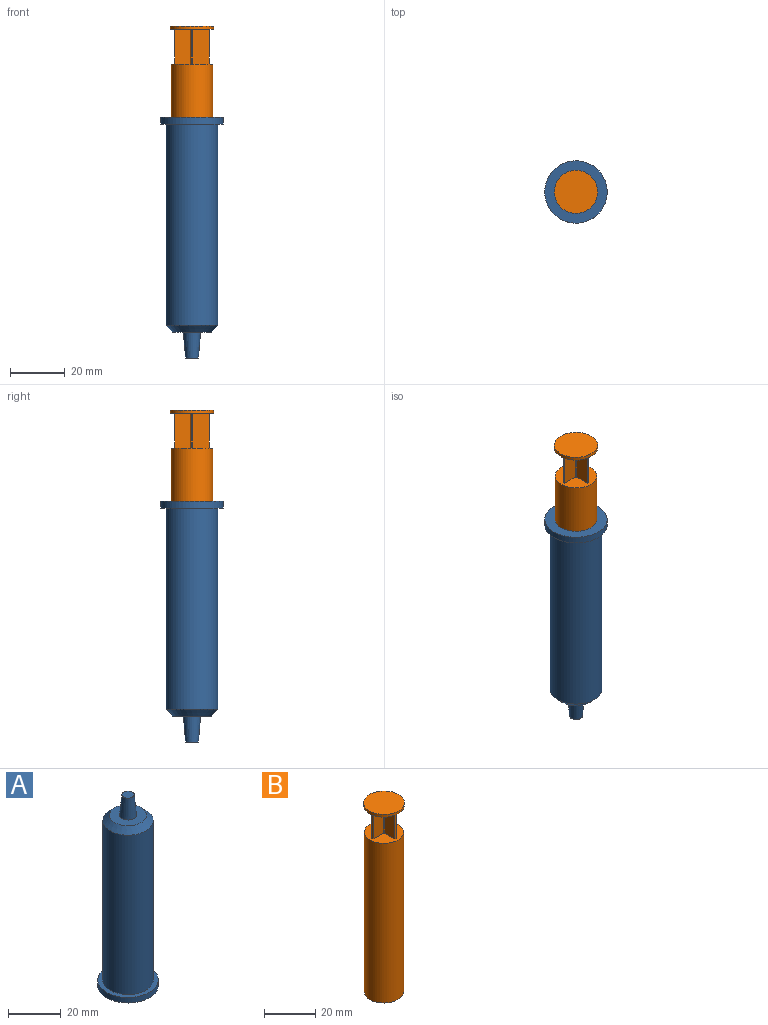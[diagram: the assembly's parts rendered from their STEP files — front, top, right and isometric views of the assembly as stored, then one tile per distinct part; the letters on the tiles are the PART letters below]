
ASSEMBLY  parts=2 mates=1
PART A: 10 faces, bbox 22.9x22.9x88.3 mm
  f0: cylinder r=9.53mm len=73.66mm, axis (0,0,-1), area 4408.4mm2, adj f4,f7
  f1: plane 13.97x13.97mm, normal (0,0,1), area 121.6mm2, adj f5,f7
  f2: cylinder r=11.43mm len=22.86mm, axis (0,0,1), area 182.4mm2, adj f3,f4
  f3: plane 22.86x22.86mm, normal (0,0,-1), area 228mm2, adj f2,f8
  f4: plane 22.86x22.86mm, normal (0,0,1), area 125.4mm2, adj f0,f2
  f5: cone r=3.17mm half-angle=5deg, axis (0,0,-1), area 165.7mm2, adj f1,f6
  f6: plane 4.68x4.68mm, normal (0,0,1), area 17.2mm2, adj f5
  f7: cone r=6.99mm half-angle=45deg, axis (0,0,-1), area 186.3mm2, adj f0,f1
  f8: cylinder r=7.62mm len=76.2mm, axis (0,0,-1), area 3648.3mm2, adj f3,f9
  f9: plane 15.24x15.24mm, normal (0,0,-1), area 182.4mm2, adj f8
PART B: 28 faces, bbox 15.9x15.9x90.2 mm
  f0: plane 15.24x15.24mm, normal (0,0,1), area 166.4mm2, adj f1,f3,f4,f5,f6,f7,f8,f9
  f1: cylinder r=7.62mm len=76.2mm, axis (0,0,-1), area 3648.3mm2, adj f0,f2
  f2: plane 15.24x15.24mm, normal (0,0,-1), area 182.4mm2, adj f1
  f3: plane 12.7x5.67mm, normal (-1,0,0), area 72mm2, adj f0,f4,f18,f19
  f4: cylinder r=0.75mm len=12.7mm, axis (0,0,-1), area 6.7mm2, adj f0,f3,f5,f19
  f5: plane 12.7x5.67mm, normal (0,1,0), area 72mm2, adj f0,f4,f6,f19
  f6: plane 12.7x0.64mm, normal (-1,0,0), area 8.1mm2, adj f0,f5,f7,f19
  f7: plane 12.7x5.67mm, normal (0,-1,0), area 72mm2, adj f0,f6,f8,f19
  f8: cylinder r=0.75mm len=12.7mm, axis (0,0,-1), area 6.7mm2, adj f0,f7,f9,f19
  f9: plane 12.7x5.67mm, normal (-1,0,0), area 72mm2, adj f0,f8,f10,f19
  f10: plane 12.7x0.64mm, normal (0,-1,0), area 8.1mm2, adj f0,f9,f11,f19
  f11: plane 12.7x5.67mm, normal (1,0,0), area 72mm2, adj f0,f10,f12,f19
  f12: cylinder r=0.75mm len=12.7mm, axis (0,0,-1), area 6.7mm2, adj f0,f11,f13,f19
  f13: plane 12.7x5.67mm, normal (0,-1,0), area 72mm2, adj f0,f12,f14,f19
  f14: plane 12.7x0.64mm, normal (1,0,0), area 8.1mm2, adj f0,f13,f15,f19
  f15: plane 12.7x5.67mm, normal (0,1,0), area 72mm2, adj f0,f14,f16,f19
  f16: cylinder r=0.75mm len=12.7mm, axis (0,0,-1), area 6.7mm2, adj f0,f15,f17,f19
  f17: plane 12.7x5.67mm, normal (1,0,0), area 72mm2, adj f0,f16,f18,f19
  f18: plane 12.7x0.64mm, normal (0,1,0), area 8.1mm2, adj f0,f3,f17,f19
  f19: plane 15.88x15.88mm, normal (0,0,-1), area 181.9mm2, adj f3,f4,f5,f6,f7,f8,f9,f10
  f20: cylinder r=7.94mm len=15.88mm, axis (0,0,-1), area 63.3mm2, adj f19,f21
  f21: plane 15.88x15.88mm, normal (0,0,1), area 197.9mm2, adj f20
  f22: plane 0.64x0.64mm, normal (0,0,1), area 0.4mm2, adj f23,f24,f25,f26
  f23: plane 12.7x0.64mm, normal (1,0,0), area 8.1mm2, adj f22,f24,f26,f27
  f24: plane 12.7x0.64mm, normal (0,1,0), area 8.1mm2, adj f22,f23,f25,f27
  f25: plane 12.7x0.64mm, normal (-1,0,0), area 8.1mm2, adj f22,f24,f26,f27
  f26: plane 12.7x0.64mm, normal (0,-1,0), area 8.1mm2, adj f22,f23,f25,f27
  f27: plane 0.64x0.64mm, normal (0,0,-1), area 0.4mm2, adj f23,f24,f25,f26
PLACE A rot(axis=(1,0,0),180deg) t=(-208.06,-136.85,12.45)mm
PLACE B rot(axis=(0,0,1),0deg) t=(-208.06,-136.85,34.42)mm
MATE slider A.f0 <-> B.f1  axis (0,0,1) through (-208.06,-136.85,53.09)mm
